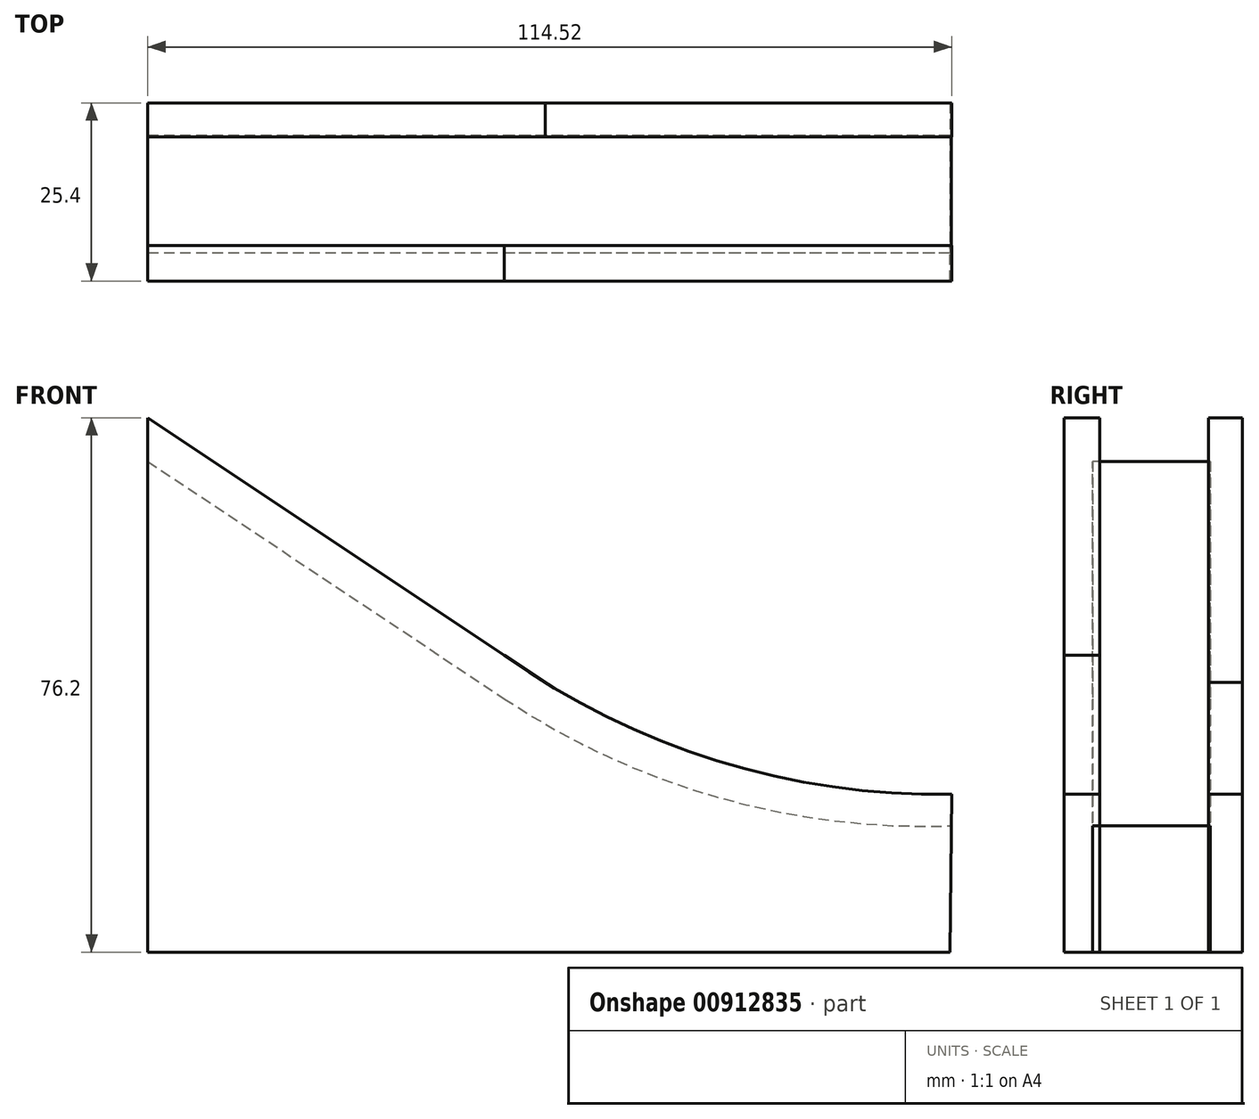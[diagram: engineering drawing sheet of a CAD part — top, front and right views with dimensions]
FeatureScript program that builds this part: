
annotation { "Feature Type Name" : "Feature", "Feature Type Description" : "" }
export const myFeature = defineFeature(function(context is Context, id is Id, definition is map)
    precondition{}
    {
        {
            var Q0;
            Q0=qCreatedBy(makeId("Front.planeOp"),FACE);
            var sketch = newSketch(context, id + "F0", { "sketchPlane" : qUnion([Q0])});
            skLineSegment(sketch, "E0", {"start": v(-50.79, -22.51) * mm, "end": v(63.51, -22.51) * mm});
            skLineSegment(sketch, "E1", {"start": v(-50.79, -22.51) * mm, "end": v(-50.79, 53.69) * mm});
            skLineSegment(sketch, "E2", {"start": v(-50.79, 53.69) * mm, "end": v(5.81, 15.95) * mm});
            skArc(sketch, "E3", {"start": v(0, 19.83) * mm, "mid": v(30.27, 4.79) * mm, "end": v(63.73, 0) * mm});
            skLineSegment(sketch, "E4", {"start": v(63.51, -22.51) * mm, "end": v(63.73, 0) * mm});
            skLineSegment(sketch, "E5", {"start": v(-50.79, 47.47) * mm, "end": v(0, 13.61) * mm});
            skArc(sketch, "E6", {"start": v(0, 13.61) * mm, "mid": v(30.42, -0.44) * mm, "end": v(63.69, -4.52) * mm});
            skSolve(sketch);
        }
        {
            var Q0;
            {var subQ8=sQuery(id+"F0.wireOp",EDGE,"E5");Q0=makeQuery(id+"F0.imprint","IMPRINT",FACE,{"disambiguationData":[TD([[makeQuery(id+"F0.imprint","IMPRINT",EDGE,{"derivedFrom":subQ8}),1.0]])]});}
            var Q1;
            {var subQ2=sQuery(id+"F0.wireOp",EDGE,"E0");Q1=makeQuery(id+"F0.imprint","IMPRINT",FACE,{"disambiguationData":[TD([[makeQuery(id+"F0.imprint","IMPRINT",EDGE,{"derivedFrom":subQ2}),1.0]])]});}
            extrude(context, id + "F1", {"entities" : qUnion([Q0, Q1]), "depth" : 5.08 * mm, "offsetDistance" : 25.4 * mm});
        }
        {
            var Q0;
            Q0 = qSketchRegion(id + "F0", true);
            extrude(context, id + "F2", {"entities" : qUnion([Q0]), "oppositeDirection" : true, "depth" : 20.32 * mm, "offsetDistance" : 25.4 * mm, "hasSecondDirection" : true, "secondDirectionOppositeDirection" : true, "secondDirectionDepth" : 15.5 * mm});
        }
        {
            var Q0;
            {var subQ2=sQuery(id+"F0.wireOp",EDGE,"E0");Q0=makeQuery(id+"F0.imprint","IMPRINT",FACE,{"disambiguationData":[TD([[makeQuery(id+"F0.imprint","IMPRINT",EDGE,{"derivedFrom":subQ2}),1.0]])]});}
            extrude(context, id + "F3", {"entities" : qUnion([Q0]), "oppositeDirection" : true, "depth" : 15.75 * mm, "offsetDistance" : 25.4 * mm, "hasSecondDirection" : true, "secondDirectionOppositeDirection" : false, "secondDirectionDepth" : 1.02 * mm});
        }
    });
